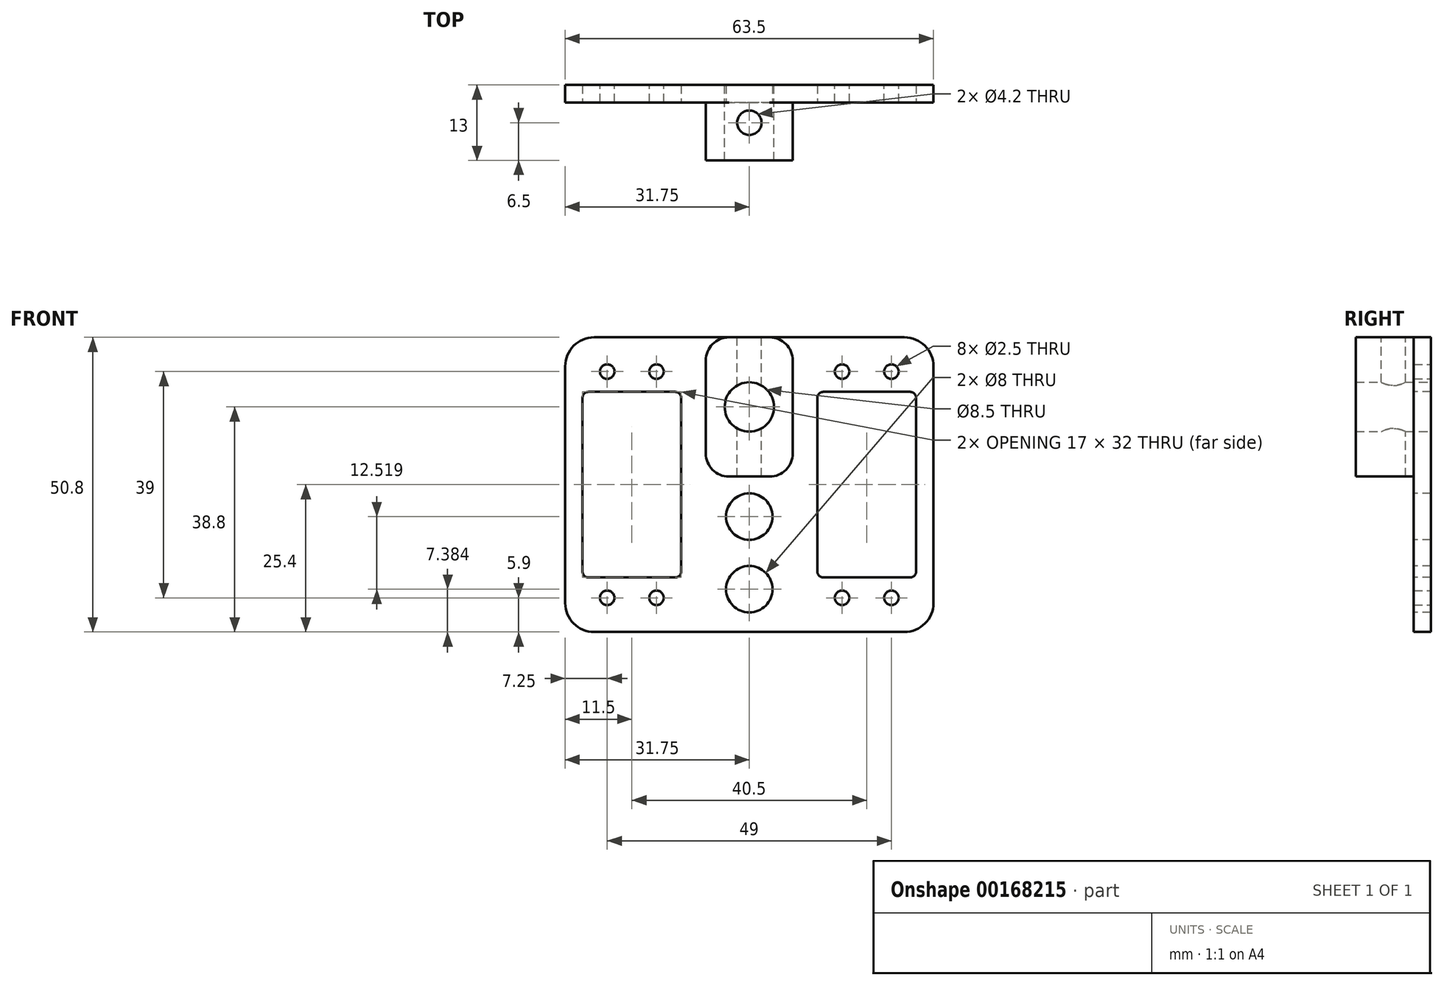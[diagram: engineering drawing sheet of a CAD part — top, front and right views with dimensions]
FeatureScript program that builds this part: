
annotation { "Feature Type Name" : "Feature", "Feature Type Description" : "" }
export const myFeature = defineFeature(function(context is Context, id is Id, definition is map)
    precondition{}
    {
        {
            var Q0;
            Q0=qCreatedBy(makeId("Front.planeOp"),FACE);
            var sketch = newSketch(context, id + "F0", { "sketchPlane" : qUnion([Q0])});
            skLineSegment(sketch, "E0.bottom", {"start": v(31.75, 25.4) * mm, "end": v(-31.75, 25.4) * mm});
            skLineSegment(sketch, "E0.top", {"start": v(31.75, -25.4) * mm, "end": v(-31.75, -25.4) * mm});
            skLineSegment(sketch, "E0.left", {"start": v(31.75, 25.4) * mm, "end": v(31.75, -25.4) * mm});
            skLineSegment(sketch, "E0.right", {"start": v(-31.75, 25.4) * mm, "end": v(-31.75, -25.4) * mm});
            skPoint(sketch, "E0.middle", {"position": v(0, 0) * mm});
            skCircle(sketch, "E1", {"center": v(0, 13.4) * mm, "radius": 4.25 * mm});
            skSolve(sketch);
        }
        {
            var Q0;
            Q0 = qSketchRegion(id + "F0", true);
            extrude(context, id + "F1", {"entities" : qUnion([Q0]), "depth" : 3 * mm, "offsetDistance" : 25 * mm});
        }
        {
            var Q0;
            Q0=makeQuery(id+"F1.opExtrude","CAP_FACE",FACE,{"disambiguationData":[OSD([sQuery(id+"F0.wireOp",EDGE,"E0.bottom"),sQuery(id+"F0.wireOp",EDGE,"E0.top"),sQuery(id+"F0.wireOp",EDGE,"E0.left"),sQuery(id+"F0.wireOp",EDGE,"E0.right"),sQuery(id+"F0.wireOp",EDGE,"E1")])],"isStart":false});
            var sketch = newSketch(context, id + "F2", { "sketchPlane" : qUnion([Q0])});
            skLineSegment(sketch, "E2.bottom", {"start": v(11.75, 16) * mm, "end": v(28.75, 16) * mm});
            skLineSegment(sketch, "E2.top", {"start": v(11.75, -16) * mm, "end": v(28.75, -16) * mm});
            skLineSegment(sketch, "E2.left", {"start": v(11.75, 16) * mm, "end": v(11.75, -16) * mm});
            skLineSegment(sketch, "E2.right", {"start": v(28.75, 16) * mm, "end": v(28.75, -16) * mm});
            skLineSegment(sketch, "E3", {"start": v(20.25, 16) * mm, "end": v(20.25, 25.4) * mm, "construction": true});
            skLineSegment(sketch, "E4", {"start": v(20.25, -16) * mm, "end": v(20.25, -25.4) * mm, "construction": true});
            skLineSegment(sketch, "E5", {"start": v(0, 0) * mm, "end": v(0, -25.4) * mm, "construction": true});
            skLineSegment(sketch, "E6.MirrorCS", {"start": v(-11.75, 16) * mm, "end": v(-11.75, -16) * mm});
            skLineSegment(sketch, "E7.MirrorCS", {"start": v(-11.75, 16) * mm, "end": v(-28.75, 16) * mm});
            skLineSegment(sketch, "E8.MirrorCS", {"start": v(-28.75, 16) * mm, "end": v(-28.75, -16) * mm});
            skLineSegment(sketch, "E9.MirrorCS", {"start": v(-11.75, -16) * mm, "end": v(-28.75, -16) * mm});
            skSolve(sketch);
        }
        {
            var Q0;
            Q0 = qSketchRegion(id + "F2", true);
            extrude(context, id + "F3", {"entities" : qUnion([Q0]), "operationType" : NewBodyOperationType.REMOVE, "endBound" : BoundingType.THROUGH_ALL, "oppositeDirection" : true, "depth" : 25 * mm, "offsetDistance" : 25 * mm});
        }
        {
            var Q0;
            Q0=makeQuery(id+"F1.opExtrude","SWEPT_EDGE",EDGE,{"disambiguationData":[OSD([sQuery(id+"F0.wireOp",EDGE,"E0.bottom"),sQuery(id+"F0.wireOp",EDGE,"E0.right")])]});
            var Q1;
            Q1=makeQuery(id+"F1.opExtrude","SWEPT_EDGE",EDGE,{"disambiguationData":[OSD([sQuery(id+"F0.wireOp",EDGE,"E0.bottom"),sQuery(id+"F0.wireOp",EDGE,"E0.left")])]});
            var Q2;
            Q2=makeQuery(id+"F1.opExtrude","SWEPT_EDGE",EDGE,{"disambiguationData":[OSD([sQuery(id+"F0.wireOp",EDGE,"E0.top"),sQuery(id+"F0.wireOp",EDGE,"E0.left")])]});
            var Q3;
            Q3=makeQuery(id+"F1.opExtrude","SWEPT_EDGE",EDGE,{"disambiguationData":[OSD([sQuery(id+"F0.wireOp",EDGE,"E0.top"),sQuery(id+"F0.wireOp",EDGE,"E0.right")])]});
            fillet(context, id + "F4", {"entities" : qUnion([Q0, Q1, Q2, Q3]), "radius" : 5 * mm, "tangentPropagation" : true, "allowEdgeOverflow" : false});
        }
        {
            var Q0;
            Q0=makeQuery(id+"F1.opExtrude","CAP_FACE",FACE,{"disambiguationData":[OSD([sQuery(id+"F0.wireOp",EDGE,"E0.bottom"),sQuery(id+"F0.wireOp",EDGE,"E0.top"),sQuery(id+"F0.wireOp",EDGE,"E0.left"),sQuery(id+"F0.wireOp",EDGE,"E0.right"),sQuery(id+"F0.wireOp",EDGE,"E1")])],"isStart":false});
            var sketch = newSketch(context, id + "F5", { "sketchPlane" : qUnion([Q0])});
            skLineSegment(sketch, "E10.bottom", {"start": v(7.5, 25.4) * mm, "end": v(-7.5, 25.4) * mm});
            skLineSegment(sketch, "E10.top", {"start": v(7.5, 1.4) * mm, "end": v(-7.5, 1.4) * mm});
            skLineSegment(sketch, "E10.left", {"start": v(7.5, 25.4) * mm, "end": v(7.5, 1.4) * mm});
            skLineSegment(sketch, "E10.right", {"start": v(-7.5, 25.4) * mm, "end": v(-7.5, 1.4) * mm});
            skPoint(sketch, "E10.middle", {"position": v(0, 13.4) * mm});
            skCircle(sketch, "E11", {"center": v(0, 13.4) * mm, "radius": 4.25 * mm});
            skSolve(sketch);
        }
        {
            var Q0;
            Q0 = qSketchRegion(id + "F5", true);
            extrude(context, id + "F6", {"entities" : qUnion([Q0]), "operationType" : NewBodyOperationType.ADD, "depth" : 10 * mm, "offsetDistance" : 25 * mm});
        }
        {
            var Q0;
            Q0=makeQuery(id+"F6.boolean.opBoolean","MERGE",FACE,{"derivedFrom":[makeQuery(id+"F1.opExtrude","SWEPT_FACE",FACE,{"disambiguationData":[OSD([sQuery(id+"F0.wireOp",EDGE,"E0.bottom")])]}),makeQuery(id+"F6.opExtrude","SWEPT_FACE",FACE,{"disambiguationData":[OSD([sQuery(id+"F5.wireOp",EDGE,"E10.bottom")])]})]});
            var sketch = newSketch(context, id + "F7", { "sketchPlane" : qUnion([Q0])});
            skLineSegment(sketch, "E12", {"start": v(0, -13) * mm, "end": v(0, 0) * mm, "construction": true});
            skPoint(sketch, "E13", {"position": v(0, -6.5) * mm});
            skSolve(sketch);
        }
        {
            var Q0;
            Q0=sQuery(id+"F7.wireOp",VERTEX,"E13");
            var Q1;
            Q1=makeQuery(id+"F1.opExtrude","SWEPT_BODY",BODY,{"disambiguationData":[OSD([sQuery(id+"F0.wireOp",EDGE,"E0.bottom"),sQuery(id+"F0.wireOp",EDGE,"E0.top"),sQuery(id+"F0.wireOp",EDGE,"E0.left"),sQuery(id+"F0.wireOp",EDGE,"E0.right"),sQuery(id+"F0.wireOp",EDGE,"E1")])]});
            hole(context, id + "F8", {"style" : HoleStyle.SIMPLE, "endStyle" : HoleEndStyle.THROUGH, "standardTappedOrClearance" : lookupTablePath({ "standard" : "ISO", "engagement" : "75%", "pitch" : "0.8 mm", "size" : "M5", "type" : "Tapped" }), "standardBlindInLast" : lookupTablePath({ "standard" : "ISO", "engagement" : "75%", "pitch" : "0.8 mm", "size" : "M5", "type" : "Tapped" }), "holeDiameter" : 4.2 * mm, "majorDiameter" : 5 * mm, "showTappedDepth" : true, "isTappedThrough" : true, "tappedDepth" : 12 * mm, "tapClearance" : 3, "locations" : qUnion([Q0]), "scope" : qUnion([Q1])});
        }
        {
            var Q0;
            Q0=makeQuery(id+"F6.opExtrude","SWEPT_EDGE",EDGE,{"disambiguationData":[OSD([sQuery(id+"F5.wireOp",EDGE,"E10.top"),sQuery(id+"F5.wireOp",EDGE,"E10.right")])]});
            var Q1;
            Q1=makeQuery(id+"F6.opExtrude","SWEPT_EDGE",EDGE,{"disambiguationData":[OSD([sQuery(id+"F5.wireOp",EDGE,"E10.top"),sQuery(id+"F5.wireOp",EDGE,"E10.left")])]});
            var Q2;
            Q2=makeQuery(id+"F6.opExtrude","SWEPT_EDGE",EDGE,{"disambiguationData":[OSD([sQuery(id+"F0.wireOp",EDGE,"E0.bottom"),sQuery(id+"F5.wireOp",EDGE,"E10.bottom"),sQuery(id+"F5.wireOp",EDGE,"E10.left")])]});
            var Q3;
            Q3=makeQuery(id+"F6.opExtrude","SWEPT_EDGE",EDGE,{"disambiguationData":[OSD([sQuery(id+"F0.wireOp",EDGE,"E0.bottom"),sQuery(id+"F5.wireOp",EDGE,"E10.bottom"),sQuery(id+"F5.wireOp",EDGE,"E10.right")])]});
            fillet(context, id + "F9", {"entities" : qUnion([Q0, Q1, Q2, Q3]), "radius" : 4 * mm, "tangentPropagation" : true, "allowEdgeOverflow" : false});
        }
        {
            var Q0;
            Q0=makeQuery(id+"F1.opExtrude","CAP_FACE",FACE,{"disambiguationData":[OSD([sQuery(id+"F0.wireOp",EDGE,"E0.bottom"),sQuery(id+"F0.wireOp",EDGE,"E0.top"),sQuery(id+"F0.wireOp",EDGE,"E0.left"),sQuery(id+"F0.wireOp",EDGE,"E0.right"),sQuery(id+"F0.wireOp",EDGE,"E1")])],"isStart":false});
            var sketch = newSketch(context, id + "F10", { "sketchPlane" : qUnion([Q0])});
            skCircle(sketch, "E14", {"center": v(0, -5.5) * mm, "radius": 4 * mm});
            skCircle(sketch, "E15", {"center": v(0, -18.02) * mm, "radius": 4 * mm});
            skLineSegment(sketch, "E16", {"start": v(0, 0) * mm, "end": v(0, -5.5) * mm, "construction": true});
            skLineSegment(sketch, "E17", {"start": v(0, -18.02) * mm, "end": v(0, -5.5) * mm, "construction": true});
            skSolve(sketch);
        }
        {
            var Q0;
            Q0 = qSketchRegion(id + "F10", true);
            extrude(context, id + "F11", {"entities" : qUnion([Q0]), "operationType" : NewBodyOperationType.REMOVE, "endBound" : BoundingType.THROUGH_ALL, "oppositeDirection" : true, "depth" : 25 * mm, "offsetDistance" : 25 * mm});
        }
        {
            var Q0;
            Q0=makeQuery(id+"F1.opExtrude","CAP_FACE",FACE,{"disambiguationData":[OSD([sQuery(id+"F0.wireOp",EDGE,"E0.bottom"),sQuery(id+"F0.wireOp",EDGE,"E0.top"),sQuery(id+"F0.wireOp",EDGE,"E0.left"),sQuery(id+"F0.wireOp",EDGE,"E0.right"),sQuery(id+"F0.wireOp",EDGE,"E1")])],"isStart":true});
            var sketch = newSketch(context, id + "F12", { "sketchPlane" : qUnion([Q0])});
            skCircle(sketch, "E18", {"center": v(-24.5, 19.5) * mm, "radius": 1.25 * mm});
            skLineSegment(sketch, "E19", {"start": v(-20.25, 16) * mm, "end": v(-20.25, 22.63) * mm, "construction": true});
            skLineSegment(sketch, "E20", {"start": v(0, 0) * mm, "end": v(0, 27.67) * mm, "construction": true});
            skLineSegment(sketch, "E21", {"start": v(0, 0) * mm, "end": v(-39.16, 0) * mm, "construction": true});
            skCircle(sketch, "E22.MirrorC", {"center": v(-16, 19.5) * mm, "radius": 1.25 * mm});
            skCircle(sketch, "E23.MirrorC", {"center": v(16, 19.5) * mm, "radius": 1.25 * mm});
            skCircle(sketch, "E24.MirrorC", {"center": v(24.5, 19.5) * mm, "radius": 1.25 * mm});
            skCircle(sketch, "E25.MirrorC", {"center": v(-24.5, -19.5) * mm, "radius": 1.25 * mm});
            skCircle(sketch, "E26.MirrorC", {"center": v(-16, -19.5) * mm, "radius": 1.25 * mm});
            skCircle(sketch, "E27.MirrorC", {"center": v(16, -19.5) * mm, "radius": 1.25 * mm});
            skCircle(sketch, "E28.MirrorC", {"center": v(24.5, -19.5) * mm, "radius": 1.25 * mm});
            skSolve(sketch);
        }
        {
            var Q0;
            Q0 = qSketchRegion(id + "F12", true);
            extrude(context, id + "F13", {"entities" : qUnion([Q0]), "operationType" : NewBodyOperationType.REMOVE, "endBound" : BoundingType.THROUGH_ALL, "oppositeDirection" : true, "depth" : 25 * mm, "offsetDistance" : 25 * mm});
        }
        {
            var Q0;
            Q0=makeQuery(id+"F3.boolean.opBoolean","COPY",EDGE,{"derivedFrom":makeQuery(id+"F3.opExtrude","SWEPT_EDGE",EDGE,{"disambiguationData":[OSD([sQuery(id+"F2.wireOp",EDGE,"E2.bottom"),sQuery(id+"F2.wireOp",EDGE,"E2.right")])]})});
            var Q1;
            Q1=makeQuery(id+"F3.boolean.opBoolean","COPY",EDGE,{"derivedFrom":makeQuery(id+"F3.opExtrude","SWEPT_EDGE",EDGE,{"disambiguationData":[OSD([sQuery(id+"F2.wireOp",EDGE,"E6.MirrorCS"),sQuery(id+"F2.wireOp",EDGE,"E7.MirrorCS")])]})});
            var Q2;
            Q2=makeQuery(id+"F3.boolean.opBoolean","COPY",EDGE,{"derivedFrom":makeQuery(id+"F3.opExtrude","SWEPT_EDGE",EDGE,{"disambiguationData":[OSD([sQuery(id+"F2.wireOp",EDGE,"E2.bottom"),sQuery(id+"F2.wireOp",EDGE,"E2.left")])]})});
            var Q3;
            Q3=makeQuery(id+"F3.boolean.opBoolean","COPY",EDGE,{"derivedFrom":makeQuery(id+"F3.opExtrude","SWEPT_EDGE",EDGE,{"disambiguationData":[OSD([sQuery(id+"F2.wireOp",EDGE,"E7.MirrorCS"),sQuery(id+"F2.wireOp",EDGE,"E8.MirrorCS")])]})});
            var Q4;
            Q4=makeQuery(id+"F3.boolean.opBoolean","COPY",EDGE,{"derivedFrom":makeQuery(id+"F3.opExtrude","SWEPT_EDGE",EDGE,{"disambiguationData":[OSD([sQuery(id+"F2.wireOp",EDGE,"E8.MirrorCS"),sQuery(id+"F2.wireOp",EDGE,"E9.MirrorCS")])]})});
            var Q5;
            Q5=makeQuery(id+"F3.boolean.opBoolean","COPY",EDGE,{"derivedFrom":makeQuery(id+"F3.opExtrude","SWEPT_EDGE",EDGE,{"disambiguationData":[OSD([sQuery(id+"F2.wireOp",EDGE,"E2.top"),sQuery(id+"F2.wireOp",EDGE,"E2.left")])]})});
            var Q6;
            Q6=makeQuery(id+"F3.boolean.opBoolean","COPY",EDGE,{"derivedFrom":makeQuery(id+"F3.opExtrude","SWEPT_EDGE",EDGE,{"disambiguationData":[OSD([sQuery(id+"F2.wireOp",EDGE,"E6.MirrorCS"),sQuery(id+"F2.wireOp",EDGE,"E9.MirrorCS")])]})});
            var Q7;
            Q7=makeQuery(id+"F3.boolean.opBoolean","COPY",EDGE,{"derivedFrom":makeQuery(id+"F3.opExtrude","SWEPT_EDGE",EDGE,{"disambiguationData":[OSD([sQuery(id+"F2.wireOp",EDGE,"E2.top"),sQuery(id+"F2.wireOp",EDGE,"E2.right")])]})});
            fillet(context, id + "F14", {"entities" : qUnion([Q0, Q1, Q2, Q3, Q4, Q5, Q6, Q7]), "radius" : 1 * mm, "tangentPropagation" : true, "allowEdgeOverflow" : false});
        }
    });
